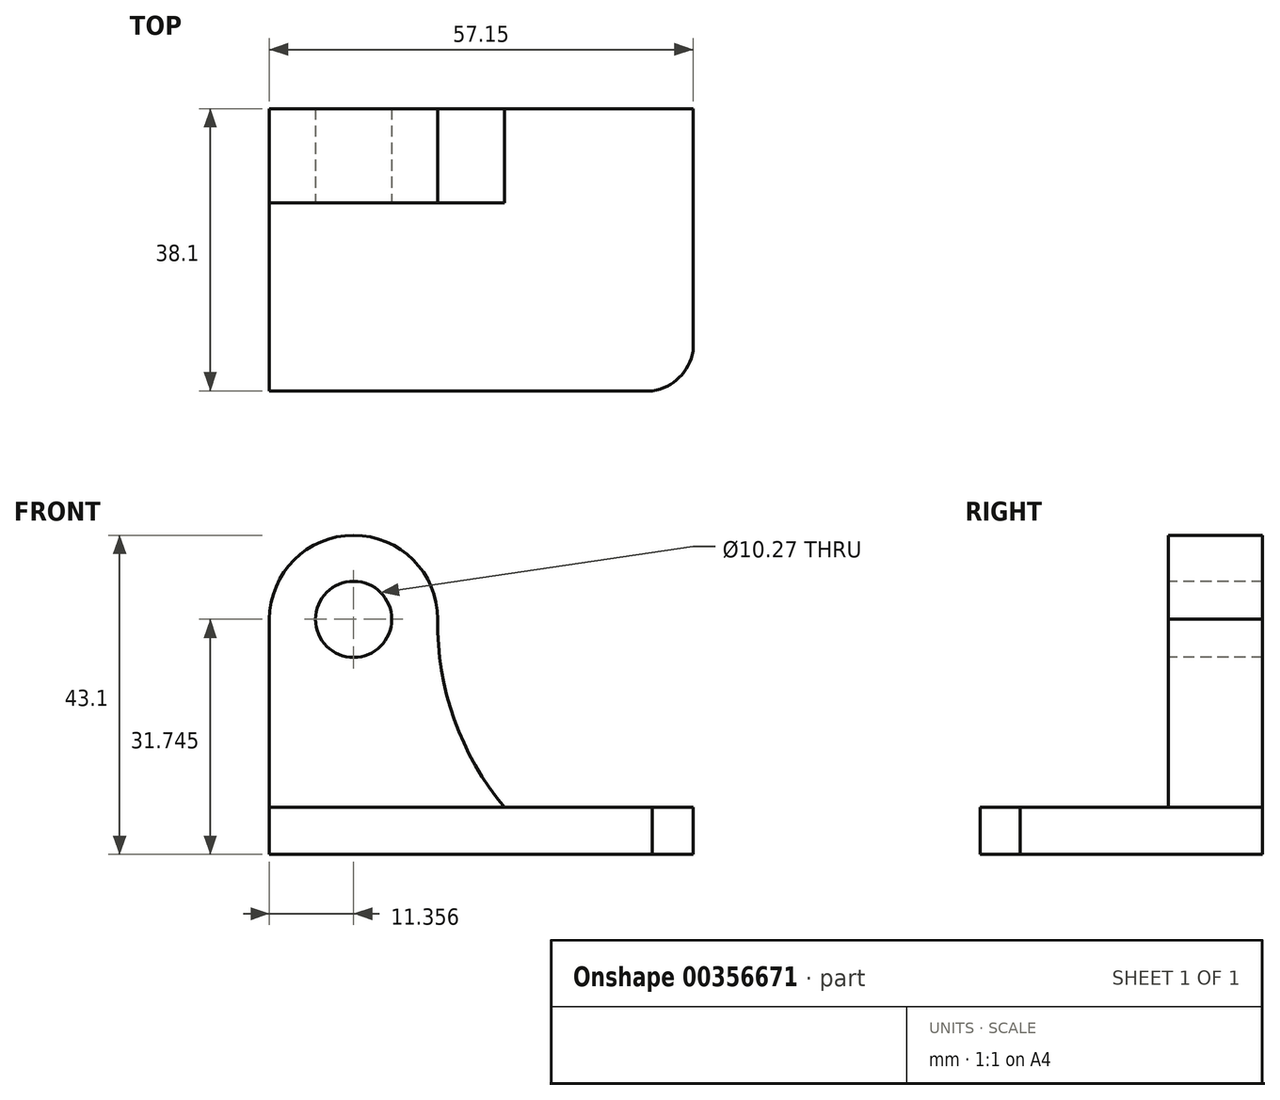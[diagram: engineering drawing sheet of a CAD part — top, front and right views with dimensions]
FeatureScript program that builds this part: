
annotation { "Feature Type Name" : "Feature", "Feature Type Description" : "" }
export const myFeature = defineFeature(function(context is Context, id is Id, definition is map)
    precondition{}
    {
        {
            var Q0;
            Q0=qCreatedBy(makeId("Front.planeOp"),FACE);
            var sketch = newSketch(context, id + "F0", { "sketchPlane" : qUnion([Q0])});
            skLineSegment(sketch, "E0.bottom", {"start": v(-22.7, -27.18) * mm, "end": v(34.44, -27.18) * mm});
            skLineSegment(sketch, "E0.top", {"start": v(-22.7, 17.27) * mm, "end": v(34.44, 17.27) * mm});
            skLineSegment(sketch, "E0.left", {"start": v(-22.7, -27.18) * mm, "end": v(-22.7, 17.27) * mm});
            skLineSegment(sketch, "E0.right", {"start": v(34.44, -27.18) * mm, "end": v(34.44, 17.27) * mm});
            skSolve(sketch);
        }
        {
            var Q0;
            Q0=makeQuery(id+"F0.imprint","IMPRINT",FACE,{"disambiguationData":[TD([[makeQuery(id+"F0.imprint","IMPRINT",EDGE,{"derivedFrom":sQuery(id+"F0.wireOp",EDGE,"E0.bottom")}),1.0]])]});
            extrude(context, id + "F1", {"entities" : qUnion([Q0]), "depth" : 38.1 * mm});
        }
        {
            var Q0;
            Q0=makeQuery(id+"F1.opExtrude","CAP_FACE",FACE,{"disambiguationData":[OSD([sQuery(id+"F0.wireOp",EDGE,"E0.bottom"),sQuery(id+"F0.wireOp",EDGE,"E0.top"),sQuery(id+"F0.wireOp",EDGE,"E0.left"),sQuery(id+"F0.wireOp",EDGE,"E0.right")])],"isStart":false});
            var sketch = newSketch(context, id + "F2", { "sketchPlane" : qUnion([Q0])});
            skLineSegment(sketch, "E1", {"start": v(-22.7, -27.18) * mm, "end": v(-22.7, 4.57) * mm});
            skArc(sketch, "E2", {"start": v(0, 4.57) * mm, "mid": v(-11.35, 15.92) * mm, "end": v(-22.7, 4.57) * mm});
            skLineSegment(sketch, "E3", {"start": v(34.44, -27.18) * mm, "end": v(34.44, -20.83) * mm});
            skLineSegment(sketch, "E4", {"start": v(34.44, -20.83) * mm, "end": v(9.04, -20.83) * mm});
            skArc(sketch, "E5", {"start": v(0, 4.57) * mm, "mid": v(2.23, -8.95) * mm, "end": v(9.04, -20.83) * mm});
            skSolve(sketch);
        }
        {
            var Q0;
            {var subQ2=sQuery(id+"F2.wireOp",EDGE,"E2");Q0=makeQuery(id+"F2.imprint","IMPRINT",FACE,{"disambiguationData":[TD([[makeQuery(id+"F2.imprint","IMPRINT",EDGE,{"derivedFrom":subQ2}),-1.0]])]});}
            extrude(context, id + "F3", {"entities" : qUnion([Q0]), "operationType" : NewBodyOperationType.REMOVE, "oppositeDirection" : true, "depth" : 50.8 * mm});
        }
        {
            var Q0;
            Q0=makeQuery(id+"F1.opExtrude","CAP_FACE",FACE,{"disambiguationData":[OSD([sQuery(id+"F0.wireOp",EDGE,"E0.bottom"),sQuery(id+"F0.wireOp",EDGE,"E0.top"),sQuery(id+"F0.wireOp",EDGE,"E0.left"),sQuery(id+"F0.wireOp",EDGE,"E0.right")])],"isStart":false});
            var sketch = newSketch(context, id + "F4", { "sketchPlane" : qUnion([Q0])});
            skCircle(sketch, "E6", {"center": v(-11.35, 4.57) * mm, "radius": 5.13 * mm});
            skSolve(sketch);
        }
        {
            var Q0;
            Q0=makeQuery(id+"F4.imprint","IMPRINT",FACE,{"disambiguationData":[TD([[makeQuery(id+"F4.imprint","IMPRINT",EDGE,{"derivedFrom":sQuery(id+"F4.wireOp",EDGE,"E6")}),1.0]])]});
            extrude(context, id + "F5", {"entities" : qUnion([Q0]), "operationType" : NewBodyOperationType.REMOVE, "oppositeDirection" : true, "depth" : 50.8 * mm});
        }
        {
            var Q0;
            Q0=makeQuery(id+"F1.opExtrude","CAP_FACE",FACE,{"disambiguationData":[OSD([sQuery(id+"F0.wireOp",EDGE,"E0.bottom"),sQuery(id+"F0.wireOp",EDGE,"E0.top"),sQuery(id+"F0.wireOp",EDGE,"E0.left"),sQuery(id+"F0.wireOp",EDGE,"E0.right")])],"isStart":false});
            var sketch = newSketch(context, id + "F6", { "sketchPlane" : qUnion([Q0])});
            skLineSegment(sketch, "E7", {"start": v(9.04, -20.83) * mm, "end": v(-22.7, -20.83) * mm});
            skSolve(sketch);
        }
        {
            var Q0;
            {var subQ1=sQuery(id+"F6.wireOp",EDGE,"E7");Q0=makeQuery(id+"F6.imprint","IMPRINT",FACE,{"disambiguationData":[TD([[makeQuery(id+"F6.imprint","IMPRINT",EDGE,{"derivedFrom":subQ1}),-1.0]])]});}
            extrude(context, id + "F7", {"entities" : qUnion([Q0]), "operationType" : NewBodyOperationType.REMOVE, "oppositeDirection" : true, "depth" : 25.4 * mm});
        }
        {
            var Q0;
            Q0=makeQuery(id+"F7.boolean.opBoolean","MERGE",FACE,{"derivedFrom":[makeQuery(id+"F3.boolean.opBoolean","COPY",FACE,{"derivedFrom":makeQuery(id+"F3.opExtrude","SWEPT_FACE",FACE,{"disambiguationData":[OSD([sQuery(id+"F2.wireOp",EDGE,"E4")])]})}),makeQuery(id+"F7.opExtrude","SWEPT_FACE",FACE,{"disambiguationData":[OSD([sQuery(id+"F6.wireOp",EDGE,"E7")])]})]});
            var sketch = newSketch(context, id + "F8", { "sketchPlane" : qUnion([Q0])});
            skArc(sketch, "E8", {"start": v(-22.7, -30.15) * mm, "mid": v(-20.7, -35.82) * mm, "end": v(-15.14, -38.1) * mm});
            skArc(sketch, "E9", {"start": v(28.98, -38.1) * mm, "mid": v(33.26, -35.53) * mm, "end": v(34.44, -30.67) * mm});
            skSolve(sketch);
        }
        {
            var Q0;
            {var subQ0=sQuery(id+"F8.wireOp",EDGE,"E8");var subQ1=sQuery(id+"F6.wireOp",EDGE,"E7");var subQ2=makeQuery(id+"F7.boolean.opBoolean","COPY",EDGE,{"derivedFrom":makeQuery(id+"F7.opExtrude","SWEPT_EDGE",EDGE,{"disambiguationData":[OSD([sQuery(id+"F0.wireOp",EDGE,"E0.left"),subQ1])]})});var subQ3=makeQuery(id+"F8.imprint","INTERSECT",VERTEX,{"disambiguationData":[OD(1.0)],"derivedFrom":[subQ2,subQ0]});Q0=makeQuery(id+"F8.imprint","IMPRINT",FACE,{"disambiguationData":[TD([[makeQuery(id+"F8.imprint","IMPRINT",EDGE,{"disambiguationData":[TD([[subQ3,-1.0]])],"derivedFrom":subQ0}),-1.0]])]});}
            var Q1;
            {var subQ0=sQuery(id+"F8.wireOp",EDGE,"E9");var subQ1=sQuery(id+"F2.wireOp",EDGE,"E4");var subQ2=makeQuery(id+"F7.boolean.opBoolean","MERGE",EDGE,{"derivedFrom":[makeQuery(id+"F3.boolean.opBoolean","COPY",EDGE,{"derivedFrom":makeQuery(id+"F3.opExtrude","CAP_EDGE",EDGE,{"disambiguationData":[OSD([subQ1])],"isStart":true})}),makeQuery(id+"F7.opExtrude","CAP_EDGE",EDGE,{"disambiguationData":[OSD([sQuery(id+"F6.wireOp",EDGE,"E7")])],"isStart":true})]});var subQ3=makeQuery(id+"F8.imprint","INTERSECT",VERTEX,{"derivedFrom":[subQ2,subQ0]});Q1=makeQuery(id+"F8.imprint","IMPRINT",FACE,{"disambiguationData":[TD([[makeQuery(id+"F8.imprint","IMPRINT",EDGE,{"disambiguationData":[TD([[subQ3,-1.0]])],"derivedFrom":subQ0}),-1.0]])]});}
            extrude(context, id + "F9", {"entities" : qUnion([Q0, Q1]), "operationType" : NewBodyOperationType.REMOVE, "oppositeDirection" : true, "depth" : 25.4 * mm});
        }
    });
